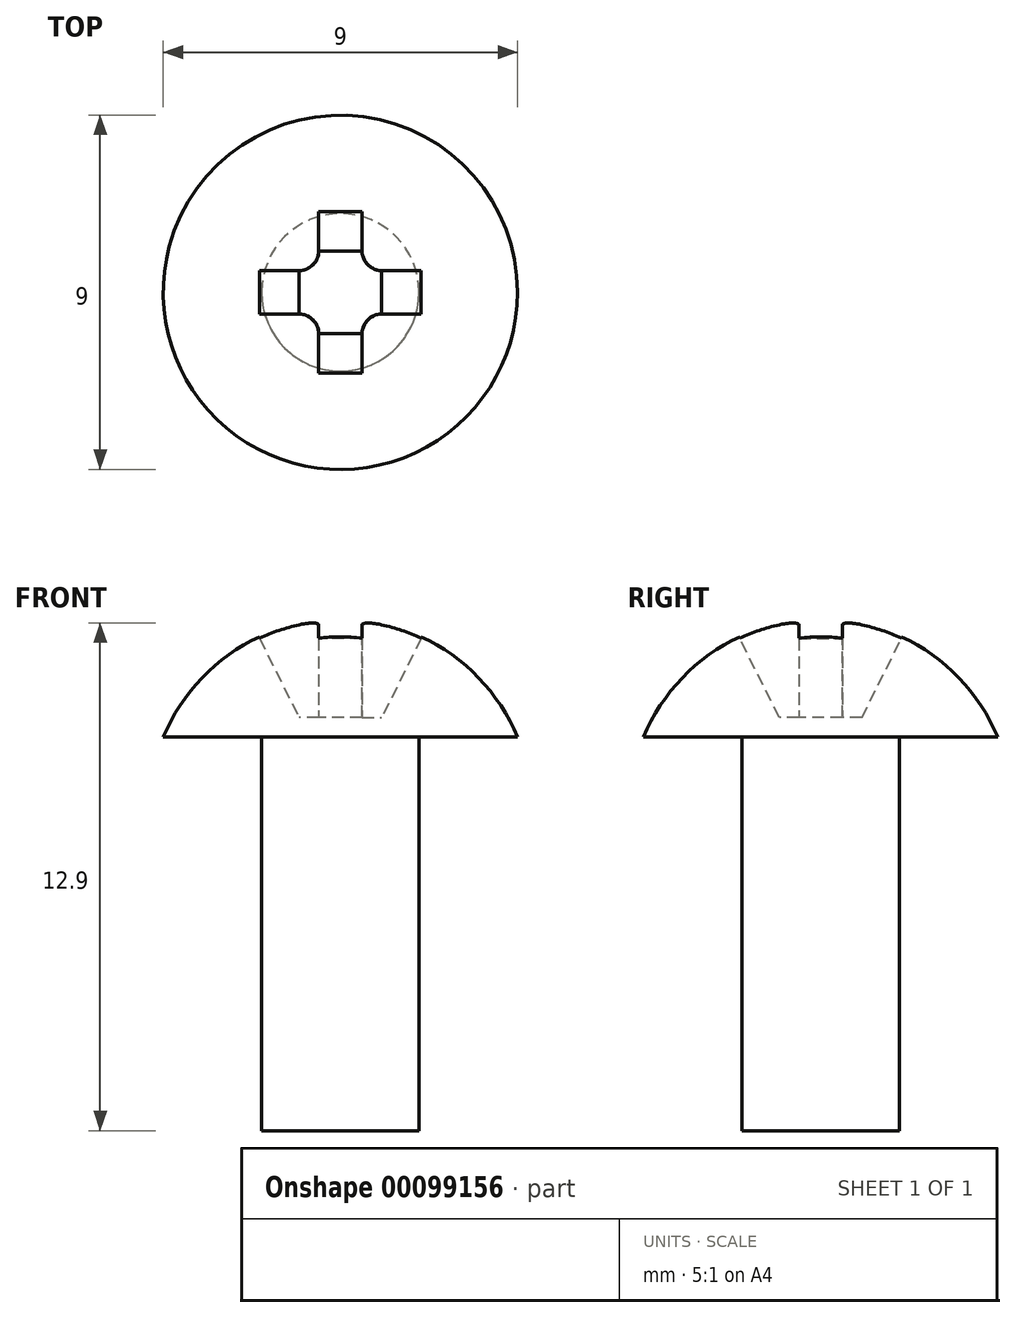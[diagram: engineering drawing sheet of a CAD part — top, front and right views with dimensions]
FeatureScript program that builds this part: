
annotation { "Feature Type Name" : "Feature", "Feature Type Description" : "" }
export const myFeature = defineFeature(function(context is Context, id is Id, definition is map)
    precondition{}
    {
        {
            var Q0;
            Q0=qCreatedBy(makeId("Front.planeOp"),FACE);
            var sketch = newSketch(context, id + "F0", { "sketchPlane" : qUnion([Q0])});
            skArc(sketch, "E0", {"start": v(0, 3) * mm, "mid": v(-2.7, 2.18) * mm, "end": v(-4.5, 0) * mm});
            skLineSegment(sketch, "E1", {"start": v(0, 3) * mm, "end": v(0, 0) * mm});
            skLineSegment(sketch, "E2", {"start": v(0, 0) * mm, "end": v(-4.5, 0) * mm});
            skSolve(sketch);
        }
        {
            var Q0;
            Q0=makeQuery(id+"F0.imprint","IMPRINT",FACE,{"disambiguationData":[TD([[makeQuery(id+"F0.imprint","IMPRINT",EDGE,{"derivedFrom":sQuery(id+"F0.wireOp",EDGE,"E0")}),1.0]])]});
            var Q1;
            Q1=sQuery(id+"F0.wireOp",EDGE,"E1");
            revolve(context, id + "F1", {"entities" : qUnion([Q0]), "axis" : qUnion([Q1]), "revolveType" : RevolveType.FULL});
        }
        {
            var Q0;
            Q0=makeQuery(id+"F1.opRevolve","SWEPT_FACE",FACE,{"disambiguationData":[OSD([sQuery(id+"F0.wireOp",EDGE,"E2")])]});
            var sketch = newSketch(context, id + "F2", { "sketchPlane" : qUnion([Q0])});
            skCircle(sketch, "E3", {"center": v(0, 0) * mm, "radius": 2 * mm});
            skSolve(sketch);
        }
        {
            var Q0;
            Q0=makeQuery(id+"F2.imprint","IMPRINT",FACE,{"disambiguationData":[TD([[makeQuery(id+"F2.imprint","IMPRINT",EDGE,{"derivedFrom":sQuery(id+"F2.wireOp",EDGE,"E3")}),1.0]])]});
            extrude(context, id + "F3", {"entities" : qUnion([Q0]), "operationType" : NewBodyOperationType.ADD, "depth" : 10 * mm});
        }
        {
            var Q0;
            Q0=makeQuery(id+"F1.opRevolve","SWEPT_FACE",FACE,{"disambiguationData":[OSD([sQuery(id+"F0.wireOp",EDGE,"E2")])]});
            var sketch = newSketch(context, id + "F4", { "sketchPlane" : qUnion([Q0])});
            skLineSegment(sketch, "E4", {"start": v(0, 2.05) * mm, "end": v(0.55, 2.05) * mm});
            skLineSegment(sketch, "E5", {"start": v(0.55, 2.05) * mm, "end": v(0.55, 0.55) * mm});
            skLineSegment(sketch, "E6", {"start": v(0.55, 0.55) * mm, "end": v(2.05, 0.55) * mm});
            skLineSegment(sketch, "E7", {"start": v(2.05, 0.55) * mm, "end": v(2.05, 0) * mm});
            skLineSegment(sketch, "E8.MirrorCS", {"start": v(0, 2.05) * mm, "end": v(-0.55, 2.05) * mm});
            skLineSegment(sketch, "E9.MirrorCS", {"start": v(-0.55, 2.05) * mm, "end": v(-0.55, 0.55) * mm});
            skLineSegment(sketch, "E10.MirrorCS", {"start": v(-0.55, 0.55) * mm, "end": v(-2.05, 0.55) * mm});
            skLineSegment(sketch, "E11.MirrorCS", {"start": v(-2.05, 0.55) * mm, "end": v(-2.05, 0) * mm});
            skLineSegment(sketch, "E12.MirrorCS", {"start": v(-2.05, -0.55) * mm, "end": v(-2.05, 0) * mm});
            skLineSegment(sketch, "E13.MirrorCS", {"start": v(-0.55, -0.55) * mm, "end": v(-2.05, -0.55) * mm});
            skLineSegment(sketch, "E14.MirrorCS", {"start": v(-0.55, -2.05) * mm, "end": v(-0.55, -0.55) * mm});
            skLineSegment(sketch, "E15.MirrorCS", {"start": v(0, -2.05) * mm, "end": v(-0.55, -2.05) * mm});
            skLineSegment(sketch, "E16.MirrorCS", {"start": v(0, -2.05) * mm, "end": v(0.55, -2.05) * mm});
            skLineSegment(sketch, "E17.MirrorCS", {"start": v(0.55, -2.05) * mm, "end": v(0.55, -0.55) * mm});
            skLineSegment(sketch, "E18.MirrorCS", {"start": v(0.55, -0.55) * mm, "end": v(2.05, -0.55) * mm});
            skLineSegment(sketch, "E19.MirrorCS", {"start": v(2.05, -0.55) * mm, "end": v(2.05, 0) * mm});
            skSolve(sketch);
        }
        {
            var Q0;
            Q0 = qSketchRegion(id + "F4", true);
            extrude(context, id + "F5", {"entities" : qUnion([Q0]), "operationType" : NewBodyOperationType.REMOVE, "endBound" : BoundingType.THROUGH_ALL, "oppositeDirection" : true, "depth" : 25.4 * mm, "hasSecondDirection" : true, "secondDirectionOppositeDirection" : true, "secondDirectionDepth" : .5 * mm});
        }
        {
            var Q0;
            Q0=makeQuery(id+"F5.boolean.opBoolean","COPY",EDGE,{"derivedFrom":makeQuery(id+"F5.opExtrude","CAP_EDGE",EDGE,{"disambiguationData":[OSD([sQuery(id+"F4.wireOp",EDGE,"E7"),sQuery(id+"F4.wireOp",EDGE,"E19.MirrorCS")])],"isStart":true})});
            var Q1;
            Q1=makeQuery(id+"F5.boolean.opBoolean","COPY",EDGE,{"derivedFrom":makeQuery(id+"F5.opExtrude","CAP_EDGE",EDGE,{"disambiguationData":[OSD([sQuery(id+"F4.wireOp",EDGE,"E15.MirrorCS"),sQuery(id+"F4.wireOp",EDGE,"E16.MirrorCS")])],"isStart":true})});
            var Q2;
            Q2=makeQuery(id+"F5.boolean.opBoolean","COPY",EDGE,{"derivedFrom":makeQuery(id+"F5.opExtrude","CAP_EDGE",EDGE,{"disambiguationData":[OSD([sQuery(id+"F4.wireOp",EDGE,"E4"),sQuery(id+"F4.wireOp",EDGE,"E8.MirrorCS")])],"isStart":true})});
            var Q3;
            Q3=makeQuery(id+"F5.boolean.opBoolean","COPY",EDGE,{"derivedFrom":makeQuery(id+"F5.opExtrude","CAP_EDGE",EDGE,{"disambiguationData":[OSD([sQuery(id+"F4.wireOp",EDGE,"E11.MirrorCS"),sQuery(id+"F4.wireOp",EDGE,"E12.MirrorCS")])],"isStart":true})});
            chamfer(context, id + "F6", {"entities" : qUnion([Q0, Q1, Q2, Q3]), "chamferType" : ChamferType.TWO_OFFSETS, "width1" : 2 * mm, "oppositeDirection" : false, "width2" : 1 * mm, "tangentPropagation" : true});
        }
        {
            var Q0;
            Q0=makeQuery(id+"F5.boolean.opBoolean","COPY",EDGE,{"derivedFrom":makeQuery(id+"F5.opExtrude","SWEPT_EDGE",EDGE,{"disambiguationData":[OSD([sQuery(id+"F4.wireOp",EDGE,"E5"),sQuery(id+"F4.wireOp",EDGE,"E6")])]})});
            var Q1;
            Q1=makeQuery(id+"F5.boolean.opBoolean","COPY",EDGE,{"derivedFrom":makeQuery(id+"F5.opExtrude","SWEPT_EDGE",EDGE,{"disambiguationData":[OSD([sQuery(id+"F4.wireOp",EDGE,"E17.MirrorCS"),sQuery(id+"F4.wireOp",EDGE,"E18.MirrorCS")])]})});
            var Q2;
            Q2=makeQuery(id+"F5.boolean.opBoolean","COPY",EDGE,{"derivedFrom":makeQuery(id+"F5.opExtrude","SWEPT_EDGE",EDGE,{"disambiguationData":[OSD([sQuery(id+"F4.wireOp",EDGE,"E9.MirrorCS"),sQuery(id+"F4.wireOp",EDGE,"E10.MirrorCS")])]})});
            var Q3;
            Q3=makeQuery(id+"F5.boolean.opBoolean","COPY",EDGE,{"derivedFrom":makeQuery(id+"F5.opExtrude","SWEPT_EDGE",EDGE,{"disambiguationData":[OSD([sQuery(id+"F4.wireOp",EDGE,"E13.MirrorCS"),sQuery(id+"F4.wireOp",EDGE,"E14.MirrorCS")])]})});
            fillet(context, id + "F7", {"entities" : qUnion([Q0, Q1, Q2, Q3]), "radius" : .5 * mm, "tangentPropagation" : true, "allowEdgeOverflow" : false});
        }
    });
